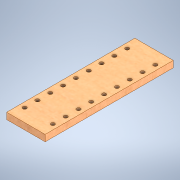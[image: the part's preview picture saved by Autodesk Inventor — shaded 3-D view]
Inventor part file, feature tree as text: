
AUTODESK INVENTOR PART (.ipt)
format: ipt  version: 2022 (Build 260153000, 153)  size: 146,944 bytes
history: native  units: mm
features: extrude x2, sketch x2
ambient origin geometry x8: Origin, YZ Plane, XZ Plane, XY Plane, X Axis, Y Axis, Z Axis, Center Point
bodies: Solid1 (feature_tree)
feature tree (4):
  extrude  "Extrusion1"  Depth=100.0mm
  extrude  "Extrusion2"  Depth=5.0mm
  sketch  "Sketch1"  dims[d0=30.0mm d1=100.0mm]
  sketch  "Sketch2"  dims[d2=5.0mm d3=0.0mm d4=3.0mm d5=10.0mm d6=4.0mm d7=90.0mm d9=10.0mm d10=20.0mm d12=22.0mm d15=5.0mm d16=0.0mm]
